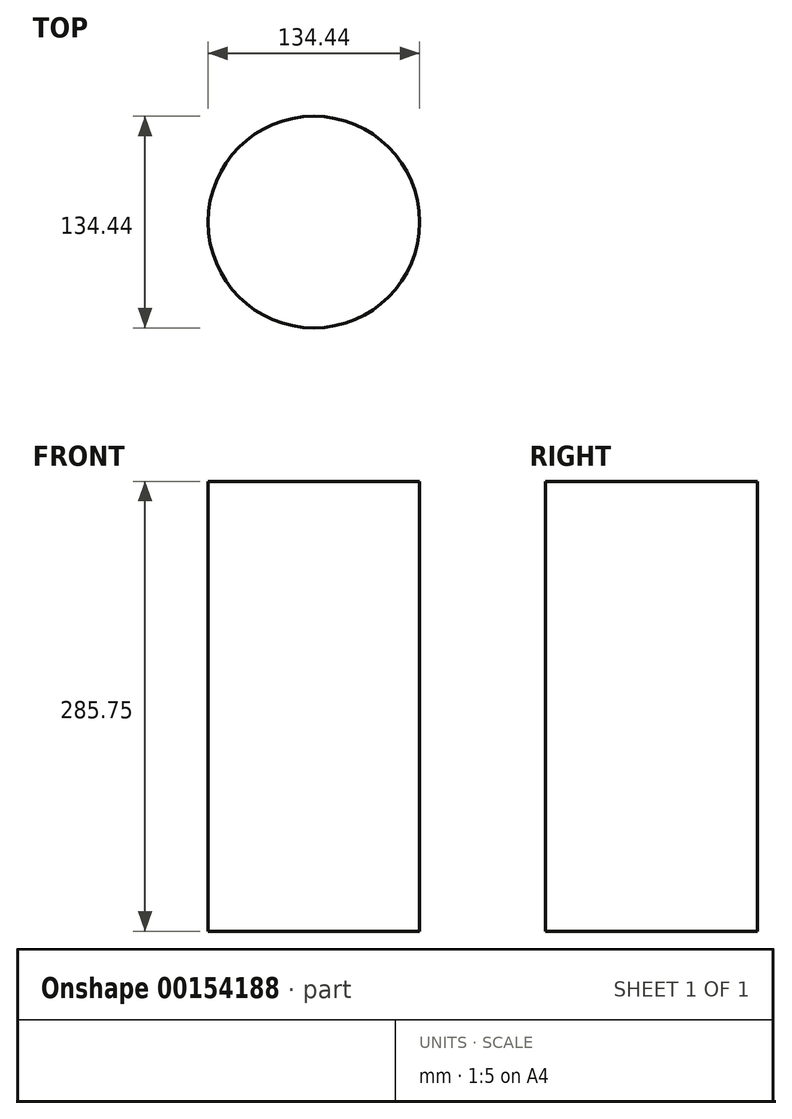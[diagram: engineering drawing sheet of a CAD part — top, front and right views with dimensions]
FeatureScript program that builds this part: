
annotation { "Feature Type Name" : "Feature", "Feature Type Description" : "" }
export const myFeature = defineFeature(function(context is Context, id is Id, definition is map)
    precondition{}
    {
        {
            var Q0;
            Q0=qCreatedBy(makeId("Top.planeOp"),FACE);
            var sketch = newSketch(context, id + "F0", { "sketchPlane" : qUnion([Q0])});
            skCircle(sketch, "E0", {"center": v(0, 0) * mm, "radius": 67.22 * mm});
            skSolve(sketch);
        }
        {
            var Q0;
            Q0 = qSketchRegion(id + "F0", true);
            extrude(context, id + "F1", {"entities" : qUnion([Q0]), "depth" : 285.75 * mm});
        }
    });
